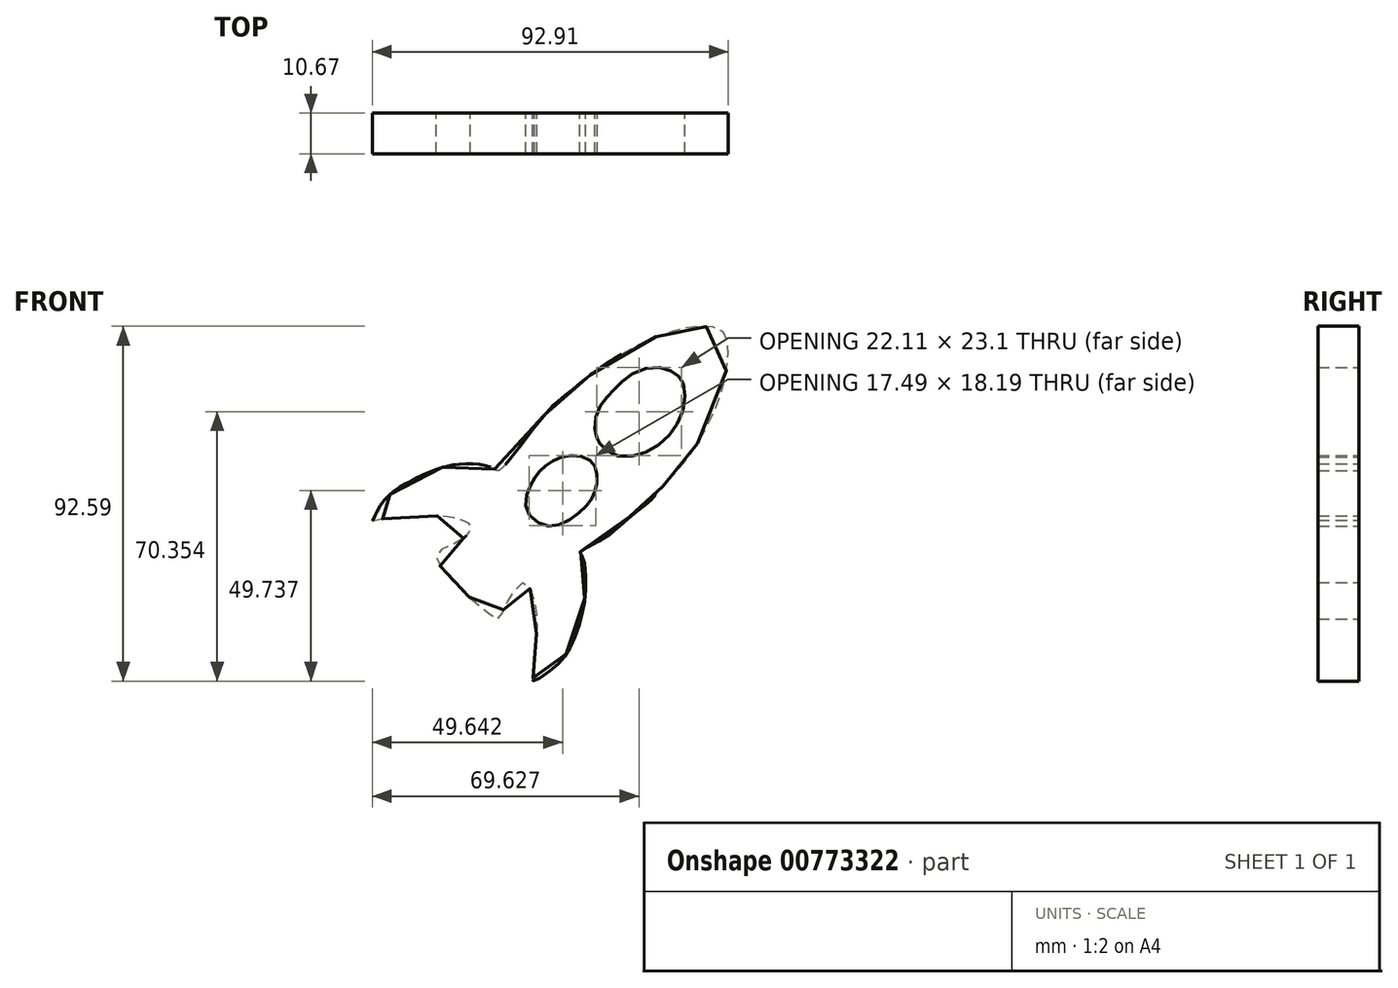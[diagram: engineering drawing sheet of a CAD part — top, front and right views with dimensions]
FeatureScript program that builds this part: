
annotation { "Feature Type Name" : "Feature", "Feature Type Description" : "" }
export const myFeature = defineFeature(function(context is Context, id is Id, definition is map)
    precondition{}
    {
        {
            var Q0;
            Q0=qCreatedBy(makeId("Front.planeOp"),FACE);
            var sketch = newSketch(context, id + "F0", { "sketchPlane" : qUnion([Q0])});
            skFitSpline(sketch, "E0", {"points": [v(-21.41, -9.55) * mm, v(-26.37, -12.13) * mm, v(-28.58, -14.24) * mm, v(-25.93, -18.93) * mm, v(-25.33, -19.47) * mm, v(-23.4, -21.69) * mm, v(-15.08, -29.01) * mm, v(-12.3, -30.64) * mm, v(-10.83, -27.92) * mm, v(-7.41, -22.4) * mm, v(-5.24, -21.2) * mm, v(-2.88, -26.34) * mm, v(-2.32, -31.14) * mm, v(-2.48, -35.42) * mm, v(-2.94, -42.7) * mm, v(-3, -45.11) * mm, v(-3.33, -46.82) * mm, v(1.89, -43.6) * mm, v(5.92, -39) * mm, v(9.2, -30.65) * mm, v(10.43, -21.93) * mm, v(9.45, -14.02) * mm, v(8.9, -13.34) * mm, v(15.37, -9.47) * mm, v(21.92, -4.02) * mm, v(27.06, 0) * mm, v(29.1, 2.28) * mm, v(33.6, 7.26) * mm, v(37.54, 12.07) * mm, v(44.69, 25.19) * mm, v(47.58, 37.58) * mm, v(46.05, 44.48) * mm, v(36.59, 45.25) * mm, v(30.1, 43.37) * mm, v(28.37, 42.83) * mm, v(15.48, 35.78) * mm, v(6.66, 28.93) * mm, v(0, 22.93) * mm, v(-12.28, 8.09) * mm, v(-13.54, 8.66) * mm, v(-20.28, 9.85) * mm, v(-27.7, 8.67) * mm, v(-35.27, 5.28) * mm, v(-42.37, 0) * mm, v(-45.06, -4.71) * mm, v(-45.24, -4.9) * mm, v(-41.01, -4.32) * mm, v(-33.14, -3.84) * mm, v(-26.32, -3.84) * mm, v(-19.8, -6.18) * mm, v(-21.41, -9.55) * mm]});
            skPoint(sketch, "E1.4.internal.snap0", {"position": v(58.55, -1.42) * mm});
            skFitSpline(sketch, "E2", {"points": [v(-3.98, 4.3) * mm, v(-4.98, -2.06) * mm, v(0, -6.3) * mm, v(6.54, -4.56) * mm, v(11.53, 0) * mm, v(13.04, 3.14) * mm, v(13.32, 7.76) * mm, v(11.58, 10.7) * mm, v(6.62, 12) * mm, v(1.38, 10.33) * mm, v(-1.63, 7.76) * mm, v(-3.98, 4.3) * mm]});
            skFitSpline(sketch, "E3", {"points": [v(13.33, 16.65) * mm, v(14.08, 15.15) * mm, v(17.93, 12.15) * mm, v(25.44, 12.62) * mm, v(32.1, 17.21) * mm, v(35.85, 23.88) * mm, v(35.85, 31.1) * mm, v(33.88, 33.35) * mm, v(29.28, 35.04) * mm, v(21.78, 32.8) * mm, v(17.93, 29.22) * mm, v(14.77, 25.7) * mm, v(12.86, 20.6) * mm, v(13.33, 16.65) * mm]});
            skFitSpline(sketch, "E4", {"points": [v(-2.34, 1.07) * mm, v(-1.68, -2.96) * mm, v(3.49, -3.36) * mm, v(6.54, -2.04) * mm, v(8.93, 0) * mm, v(10.25, 3.14) * mm, v(10.78, 5.8) * mm, v(10.24, 8.2) * mm, v(8.17, 9.8) * mm, v(6.14, 9.77) * mm, v(2.3, 8.58) * mm, v(-0.93, 5.3) * mm, v(-2.34, 1.07) * mm]});
            skFitSpline(sketch, "E5", {"points": [v(20.81, 26.79) * mm, v(17.22, 20.52) * mm, v(18.1, 16.22) * mm, v(21.37, 15.21) * mm, v(26.98, 17.74) * mm, v(30.42, 21.2) * mm, v(32.14, 24.11) * mm, v(32.66, 27.29) * mm, v(31.86, 30.31) * mm, v(28.44, 31.5) * mm, v(24.33, 30.06) * mm, v(20.81, 26.79) * mm]});
            skSolve(sketch);
        }
        {
            var Q0;
            Q0 = qSketchRegion(id + "F0", true);
            extrude(context, id + "F1", {"entities" : qUnion([Q0]), "depth" : 10.67 * mm, "offsetDistance" : 25.4 * mm});
        }
    });
